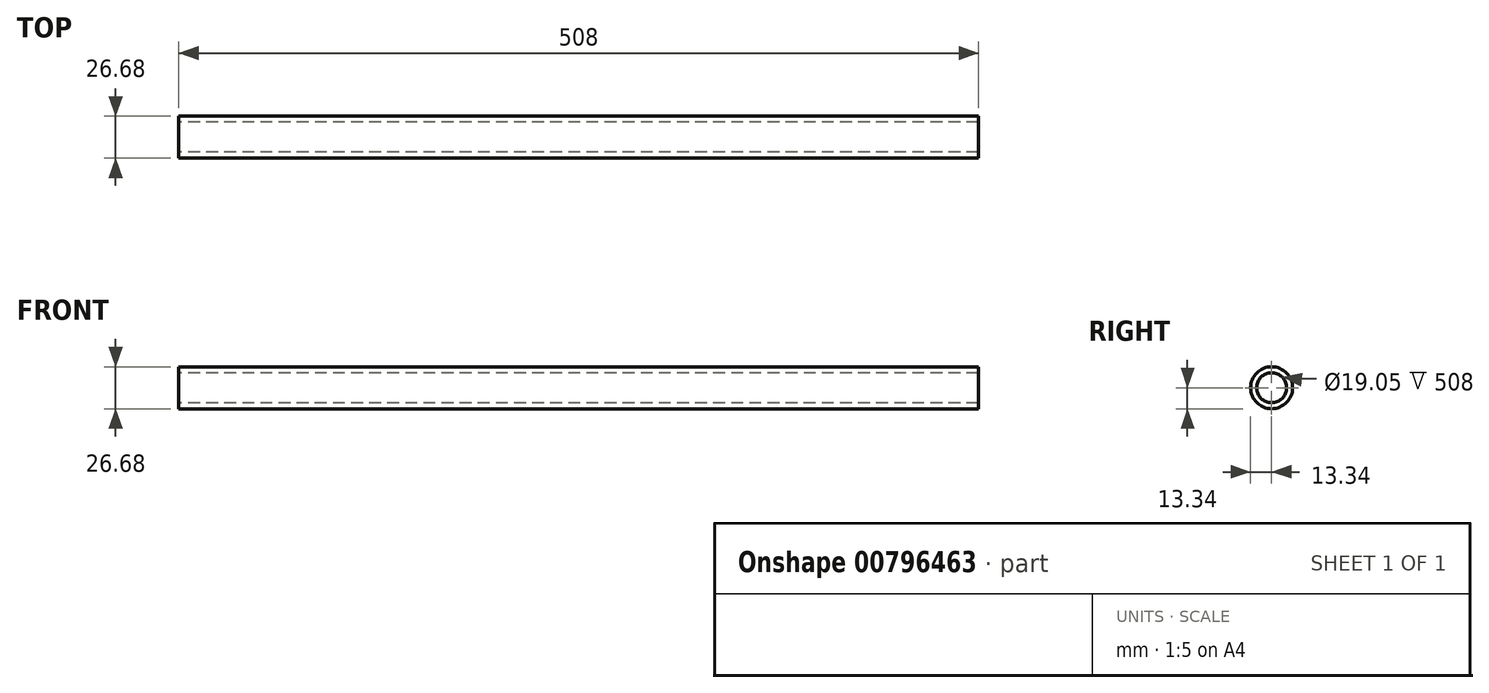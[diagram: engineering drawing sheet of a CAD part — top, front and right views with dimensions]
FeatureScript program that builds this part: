
annotation { "Feature Type Name" : "Feature", "Feature Type Description" : "" }
export const myFeature = defineFeature(function(context is Context, id is Id, definition is map)
    precondition{}
    {
        {
            var Q0;
            Q0=qCreatedBy(makeId("Right.planeOp"),FACE);
            var sketch = newSketch(context, id + "F0", { "sketchPlane" : qUnion([Q0])});
            skCircle(sketch, "E0", {"center": v(0, 0) * mm, "radius": 9.53 * mm});
            skCircle(sketch, "E1.0", {"center": v(0, 0) * mm, "radius": 13.33 * mm});
            skSolve(sketch);
        }
        {
            var Q0;
            Q0=qSketchRegion(id+"F0",true);
            extrude(context, id + "F1", {"entities" : qUnion([Q0]), "depth" : 508 * mm, "offsetDistance" : 25.4 * mm});
        }
    });
